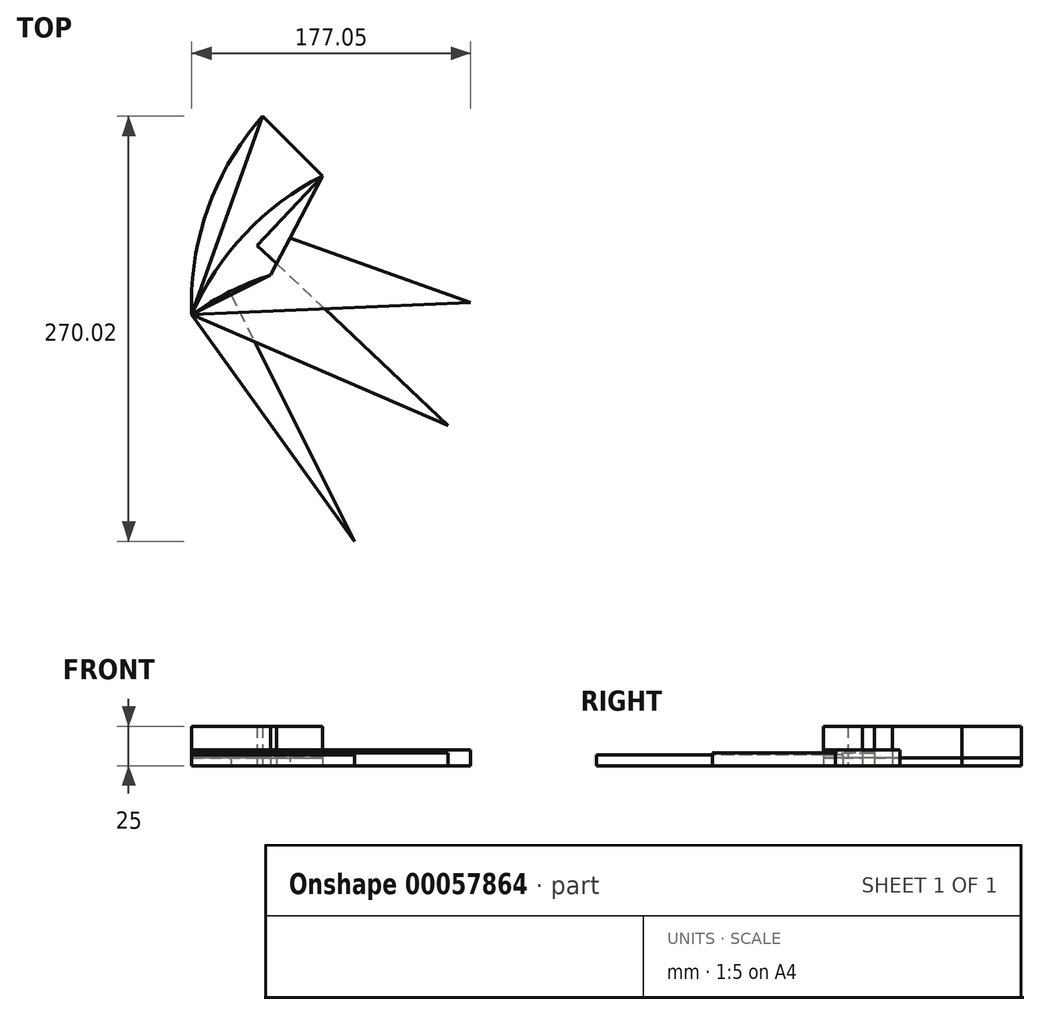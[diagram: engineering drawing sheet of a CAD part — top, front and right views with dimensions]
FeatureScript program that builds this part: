
annotation { "Feature Type Name" : "Feature", "Feature Type Description" : "" }
export const myFeature = defineFeature(function(context is Context, id is Id, definition is map)
    precondition{}
    {
        {
            var Q0;
            Q0=qCreatedBy(makeId("Top.planeOp"),FACE);
            var sketch = newSketch(context, id + "F0", { "sketchPlane" : qUnion([Q0])});
            skCircle(sketch, "E0", {"center": v(0, 0) * mm, "radius": 150 * mm});
            skLineSegment(sketch, "E1", {"start": v(0, 0) * mm, "end": v(173.9, 0) * mm});
            skLineSegment(sketch, "E2", {"start": v(0, 0) * mm, "end": v(0, 191.6) * mm});
            skPoint(sketch, "E3", {"position": v(50, 25) * mm});
            skPoint(sketch, "E4", {"position": v(83, 88) * mm});
            skLineSegment(sketch, "E5", {"start": v(0, 0) * mm, "end": v(50, 25) * mm});
            skLineSegment(sketch, "E6", {"start": v(0, 0) * mm, "end": v(83, 88) * mm});
            skPoint(sketch, "E7", {"position": v(41.5, 44) * mm});
            skPoint(sketch, "E8", {"position": v(25, 12.5) * mm});
            skLineSegment(sketch, "E9", {"start": v(25, 12.5) * mm, "end": v(103.26, -144.02) * mm});
            skLineSegment(sketch, "E10", {"start": v(41.5, 44) * mm, "end": v(162.68, -70.3) * mm});
            skLineSegment(sketch, "E11", {"start": v(0, 0) * mm, "end": v(103.26, -144.02) * mm});
            skLineSegment(sketch, "E12", {"start": v(50, 25) * mm, "end": v(103.26, -144.02) * mm, "construction": true});
            skLineSegment(sketch, "E13", {"start": v(0, 0) * mm, "end": v(162.68, -70.3) * mm});
            skLineSegment(sketch, "E14", {"start": v(83, 88) * mm, "end": v(162.68, -70.3) * mm, "construction": true});
            skArc(sketch, "E15", {"start": v(0, 0) * mm, "mid": v(24, 14.48) * mm, "end": v(50, 25) * mm});
            skArc(sketch, "E16", {"start": v(83, 88) * mm, "mid": v(33.76, 51.3) * mm, "end": v(0, 0) * mm});
            skLineSegment(sketch, "E17", {"start": v(50, 25) * mm, "end": v(83, 88) * mm});
            skLineSegment(sketch, "E18", {"start": v(50, 25) * mm, "end": v(0, 25) * mm, "construction": true});
            skLineSegment(sketch, "E19", {"start": v(83, 88) * mm, "end": v(0, 88) * mm, "construction": true});
            skLineSegment(sketch, "E20", {"start": v(50, 25) * mm, "end": v(50, 0) * mm, "construction": true});
            skLineSegment(sketch, "E21", {"start": v(83, 88) * mm, "end": v(83, 0) * mm, "construction": true});
            skPoint(sketch, "E22", {"position": v(45, 126) * mm});
            skLineSegment(sketch, "E23", {"start": v(45, 126) * mm, "end": v(0, 0) * mm});
            skPoint(sketch, "E24.positionSnap0", {"position": v(22.5, 63) * mm});
            skLineSegment(sketch, "E25", {"start": v(22.5, 63) * mm, "end": v(177.05, 7.8) * mm});
            skLineSegment(sketch, "E26", {"start": v(0, 0) * mm, "end": v(177.05, 7.8) * mm});
            skLineSegment(sketch, "E27", {"start": v(45, 126) * mm, "end": v(177.05, 7.8) * mm, "construction": true});
            skLineSegment(sketch, "E28", {"start": v(45, 126) * mm, "end": v(0, 126) * mm, "construction": true});
            skPoint(sketch, "E29.endSnap0", {"position": v(50, 12.5) * mm});
            skArc(sketch, "E30", {"start": v(0, 0) * mm, "mid": v(10.15, 67.4) * mm, "end": v(45, 126) * mm});
            skLineSegment(sketch, "E31", {"start": v(22.5, 63) * mm, "end": v(10.15, 67.4) * mm});
            skLineSegment(sketch, "E32", {"start": v(45, 126) * mm, "end": v(83, 88) * mm});
            skCircle(sketch, "E33", {"center": v(0, 0) * mm, "radius": 177.22 * mm, "construction": true});
            skPoint(sketch, "E34", {"position": v(66.5, 56.5) * mm});
            skPoint(sketch, "E35", {"position": v(64, 107) * mm});
            skLineSegment(sketch, "E36", {"start": v(66.5, 56.5) * mm, "end": v(0, 0) * mm, "construction": true});
            skLineSegment(sketch, "E37", {"start": v(64, 107) * mm, "end": v(0, 0) * mm, "construction": true});
            skPoint(sketch, "E38", {"position": v(33.25, 28.25) * mm});
            skPoint(sketch, "E39", {"position": v(32, 53.5) * mm});
            skLineSegment(sketch, "E40", {"start": v(32, 53.5) * mm, "end": v(174.37, -31.65) * mm, "construction": true});
            skLineSegment(sketch, "E41", {"start": v(33.25, 28.25) * mm, "end": v(144.46, -102.65) * mm, "construction": true});
            skLineSegment(sketch, "E42", {"start": v(0, 0) * mm, "end": v(174.37, -31.65) * mm, "construction": true});
            skLineSegment(sketch, "E43", {"start": v(0, 0) * mm, "end": v(144.46, -102.65) * mm, "construction": true});
            skSolve(sketch);
        }
        {
            var Q0;
            {var subQ3=sQuery(id+"F0.wireOp",EDGE,"E31");Q0=makeQuery(id+"F0.imprint","IMPRINT",FACE,{"disambiguationData":[TD([[makeQuery(id+"F0.imprint","IMPRINT",EDGE,{"derivedFrom":subQ3}),-1.0]])]});}
            var Q1;
            {var subQ5=sQuery(id+"F0.wireOp",EDGE,"E31");Q1=makeQuery(id+"F0.imprint","IMPRINT",FACE,{"disambiguationData":[TD([[makeQuery(id+"F0.imprint","IMPRINT",EDGE,{"derivedFrom":subQ5}),1.0]])]});}
            var Q2;
            {var subQ1=sQuery(id+"F0.wireOp",EDGE,"E6");var subQ3=makeQuery(id+"F0.imprint","INTERSECT",VERTEX,{"derivedFrom":[subQ1,sQuery(id+"F0.wireOp",EDGE,"E10")]});Q2=makeQuery(id+"F0.imprint","IMPRINT",FACE,{"disambiguationData":[TD([[makeQuery(id+"F0.imprint","IMPRINT",EDGE,{"disambiguationData":[TD([[subQ3,-1.0]])],"derivedFrom":subQ1}),1.0]])]});}
            var Q3;
            {var subQ1=sQuery(id+"F0.wireOp",EDGE,"E6");var subQ3=sQuery(id+"F0.wireOp",EDGE,"E25");var subQ4=makeQuery(id+"F0.imprint","INTERSECT",VERTEX,{"derivedFrom":[subQ1,subQ3]});Q3=makeQuery(id+"F0.imprint","IMPRINT",FACE,{"disambiguationData":[TD([[makeQuery(id+"F0.imprint","IMPRINT",EDGE,{"disambiguationData":[TD([[subQ4,1.0]])],"derivedFrom":subQ3}),1.0]])]});}
            var Q4;
            {var subQ0=sQuery(id+"F0.wireOp",EDGE,"E15");Q4=makeQuery(id+"F0.imprint","IMPRINT",FACE,{"disambiguationData":[TD([[makeQuery(id+"F0.imprint","IMPRINT",EDGE,{"derivedFrom":subQ0}),-1.0]])]});}
            extrude(context, id + "F1", {"entities" : qUnion([Q0, Q1, Q2, Q3, Q4]), "depth" : 25 * mm, "offsetDistance" : 25 * mm});
        }
        {
            var Q0;
            {var subQ0=sQuery(id+"F0.wireOp",EDGE,"E32");Q0=makeQuery(id+"F0.imprint","IMPRINT",FACE,{"disambiguationData":[TD([[makeQuery(id+"F0.imprint","IMPRINT",EDGE,{"derivedFrom":subQ0}),-1.0]])]});}
            var Q1;
            {var subQ1=sQuery(id+"F0.wireOp",EDGE,"E16");var subQ3=sQuery(id+"F0.wireOp",EDGE,"E25");var subQ4=makeQuery(id+"F0.imprint","INTERSECT",VERTEX,{"derivedFrom":[subQ1,subQ3]});Q1=makeQuery(id+"F0.imprint","IMPRINT",FACE,{"disambiguationData":[TD([[makeQuery(id+"F0.imprint","IMPRINT",EDGE,{"disambiguationData":[TD([[subQ4,1.0]])],"derivedFrom":subQ3}),-1.0]])]});}
            extrude(context, id + "F2", {"entities" : qUnion([Q0, Q1]), "depth" : 5 * mm, "offsetDistance" : 25 * mm});
        }
        {
            var Q0;
            {var subQ1=sQuery(id+"F0.wireOp",EDGE,"E6");var subQ3=sQuery(id+"F0.wireOp",EDGE,"E25");var subQ4=makeQuery(id+"F0.imprint","INTERSECT",VERTEX,{"derivedFrom":[subQ1,subQ3]});Q0=makeQuery(id+"F0.imprint","IMPRINT",FACE,{"disambiguationData":[TD([[makeQuery(id+"F0.imprint","IMPRINT",EDGE,{"disambiguationData":[TD([[subQ4,-1.0]])],"derivedFrom":subQ3}),1.0]])]});}
            var Q1;
            {var subQ0=sQuery(id+"F0.wireOp",EDGE,"E10");var subQ1=sQuery(id+"F0.wireOp",EDGE,"E6");var subQ2=makeQuery(id+"F0.imprint","INTERSECT",VERTEX,{"derivedFrom":[subQ1,subQ0]});Q1=makeQuery(id+"F0.imprint","IMPRINT",FACE,{"disambiguationData":[TD([[makeQuery(id+"F0.imprint","IMPRINT",EDGE,{"disambiguationData":[TD([[subQ2,-1.0]])],"derivedFrom":subQ1}),-1.0]])]});}
            var Q2;
            {var subQ0=sQuery(id+"F0.wireOp",EDGE,"E15");Q2=makeQuery(id+"F0.imprint","IMPRINT",FACE,{"disambiguationData":[TD([[makeQuery(id+"F0.imprint","IMPRINT",EDGE,{"derivedFrom":subQ0}),1.0]])]});}
            extrude(context, id + "F3", {"entities" : qUnion([Q0, Q1, Q2]), "depth" : 5 * mm, "offsetDistance" : 25 * mm});
        }
        {
            var Q0;
            {var subQ0=sQuery(id+"F0.wireOp",EDGE,"E11");var subQ1=sQuery(id+"F0.wireOp",EDGE,"E0");var subQ2=makeQuery(id+"F0.imprint","INTERSECT",VERTEX,{"derivedFrom":[subQ1,subQ0]});Q0=makeQuery(id+"F0.imprint","IMPRINT",FACE,{"disambiguationData":[TD([[makeQuery(id+"F0.imprint","IMPRINT",EDGE,{"disambiguationData":[TD([[subQ2,-1.0]])],"derivedFrom":subQ1}),1.0]])]});}
            var Q1;
            {var subQ1=sQuery(id+"F0.wireOp",EDGE,"E1");var subQ3=sQuery(id+"F0.wireOp",EDGE,"E9");var subQ4=makeQuery(id+"F0.imprint","INTERSECT",VERTEX,{"derivedFrom":[subQ1,subQ3]});Q1=makeQuery(id+"F0.imprint","IMPRINT",FACE,{"disambiguationData":[TD([[makeQuery(id+"F0.imprint","IMPRINT",EDGE,{"disambiguationData":[TD([[subQ4,-1.0]])],"derivedFrom":subQ3}),-1.0]])]});}
            var Q2;
            {var subQ1=sQuery(id+"F0.wireOp",EDGE,"E1");var subQ3=sQuery(id+"F0.wireOp",EDGE,"E9");var subQ4=makeQuery(id+"F0.imprint","INTERSECT",VERTEX,{"derivedFrom":[subQ1,subQ3]});Q2=makeQuery(id+"F0.imprint","IMPRINT",FACE,{"disambiguationData":[TD([[makeQuery(id+"F0.imprint","IMPRINT",EDGE,{"disambiguationData":[TD([[subQ4,1.0]])],"derivedFrom":subQ3}),-1.0]])]});}
            var Q3;
            {var subQ1=sQuery(id+"F0.wireOp",EDGE,"E5");var subQ3=sQuery(id+"F0.wireOp",EDGE,"E9");var subQ4=makeQuery(id+"F0.imprint","INTERSECT",VERTEX,{"derivedFrom":[subQ1,subQ3]});Q3=makeQuery(id+"F0.imprint","IMPRINT",FACE,{"disambiguationData":[TD([[makeQuery(id+"F0.imprint","IMPRINT",EDGE,{"disambiguationData":[TD([[subQ4,-1.0]])],"derivedFrom":subQ3}),-1.0]])]});}
            var Q4;
            {var subQ0=sQuery(id+"F0.wireOp",EDGE,"E11");var subQ1=sQuery(id+"F0.wireOp",EDGE,"E0");var subQ2=makeQuery(id+"F0.imprint","INTERSECT",VERTEX,{"derivedFrom":[subQ1,subQ0]});Q4=makeQuery(id+"F0.imprint","IMPRINT",FACE,{"disambiguationData":[TD([[makeQuery(id+"F0.imprint","IMPRINT",EDGE,{"disambiguationData":[TD([[subQ2,-1.0]])],"derivedFrom":subQ1}),-1.0]])]});}
            extrude(context, id + "F4", {"entities" : qUnion([Q0, Q1, Q2, Q3, Q4]), "depth" : 7 * mm, "offsetDistance" : 25 * mm});
        }
        {
            var Q0;
            {var subQ3=sQuery(id+"F0.wireOp",EDGE,"E13");var subQ7=sQuery(id+"F0.wireOp",EDGE,"E0");var subQ8=makeQuery(id+"F0.imprint","INTERSECT",VERTEX,{"derivedFrom":[subQ7,subQ3]});Q0=makeQuery(id+"F0.imprint","IMPRINT",FACE,{"disambiguationData":[TD([[makeQuery(id+"F0.imprint","IMPRINT",EDGE,{"disambiguationData":[TD([[subQ8,-1.0]])],"derivedFrom":subQ7}),1.0]])]});}
            var Q1;
            {var subQ0=sQuery(id+"F0.wireOp",EDGE,"E13");var subQ1=sQuery(id+"F0.wireOp",EDGE,"E0");var subQ2=makeQuery(id+"F0.imprint","INTERSECT",VERTEX,{"derivedFrom":[subQ1,subQ0]});Q1=makeQuery(id+"F0.imprint","IMPRINT",FACE,{"disambiguationData":[TD([[makeQuery(id+"F0.imprint","IMPRINT",EDGE,{"disambiguationData":[TD([[subQ2,-1.0]])],"derivedFrom":subQ1}),-1.0]])]});}
            var Q2;
            {var subQ1=sQuery(id+"F0.wireOp",EDGE,"E1");var subQ3=sQuery(id+"F0.wireOp",EDGE,"E9");var subQ4=makeQuery(id+"F0.imprint","INTERSECT",VERTEX,{"derivedFrom":[subQ1,subQ3]});Q2=makeQuery(id+"F0.imprint","IMPRINT",FACE,{"disambiguationData":[TD([[makeQuery(id+"F0.imprint","IMPRINT",EDGE,{"disambiguationData":[TD([[subQ4,-1.0]])],"derivedFrom":subQ3}),-1.0]])]});}
            var Q3;
            {var subQ1=sQuery(id+"F0.wireOp",EDGE,"E5");var subQ3=sQuery(id+"F0.wireOp",EDGE,"E9");var subQ4=makeQuery(id+"F0.imprint","INTERSECT",VERTEX,{"derivedFrom":[subQ1,subQ3]});Q3=makeQuery(id+"F0.imprint","IMPRINT",FACE,{"disambiguationData":[TD([[makeQuery(id+"F0.imprint","IMPRINT",EDGE,{"disambiguationData":[TD([[subQ4,-1.0]])],"derivedFrom":subQ3}),-1.0]])]});}
            var Q4;
            {var subQ1=sQuery(id+"F0.wireOp",EDGE,"E5");var subQ5=sQuery(id+"F0.wireOp",EDGE,"E9");var subQ6=makeQuery(id+"F0.imprint","INTERSECT",VERTEX,{"derivedFrom":[subQ1,subQ5]});Q4=makeQuery(id+"F0.imprint","IMPRINT",FACE,{"disambiguationData":[TD([[makeQuery(id+"F0.imprint","IMPRINT",EDGE,{"disambiguationData":[TD([[subQ6,-1.0]])],"derivedFrom":subQ5}),1.0]])]});}
            var Q5;
            {var subQ0=sQuery(id+"F0.wireOp",EDGE,"E9");var subQ1=sQuery(id+"F0.wireOp",EDGE,"E1");var subQ2=makeQuery(id+"F0.imprint","INTERSECT",VERTEX,{"derivedFrom":[subQ1,subQ0]});Q5=makeQuery(id+"F0.imprint","IMPRINT",FACE,{"disambiguationData":[TD([[makeQuery(id+"F0.imprint","IMPRINT",EDGE,{"disambiguationData":[TD([[subQ2,-1.0]])],"derivedFrom":subQ1}),1.0]])]});}
            var Q6;
            {var subQ1=sQuery(id+"F0.wireOp",EDGE,"E1");var subQ3=sQuery(id+"F0.wireOp",EDGE,"E9");var subQ4=makeQuery(id+"F0.imprint","INTERSECT",VERTEX,{"derivedFrom":[subQ1,subQ3]});Q6=makeQuery(id+"F0.imprint","IMPRINT",FACE,{"disambiguationData":[TD([[makeQuery(id+"F0.imprint","IMPRINT",EDGE,{"disambiguationData":[TD([[subQ4,1.0]])],"derivedFrom":subQ3}),-1.0]])]});}
            extrude(context, id + "F5", {"entities" : qUnion([Q0, Q1, Q2, Q3, Q4, Q5, Q6]), "depth" : 8 * mm, "offsetDistance" : 25 * mm});
        }
        {
            var Q0;
            {var subQ1=sQuery(id+"F0.wireOp",EDGE,"E5");var subQ3=sQuery(id+"F0.wireOp",EDGE,"E9");var subQ4=makeQuery(id+"F0.imprint","INTERSECT",VERTEX,{"derivedFrom":[subQ1,subQ3]});Q0=makeQuery(id+"F0.imprint","IMPRINT",FACE,{"disambiguationData":[TD([[makeQuery(id+"F0.imprint","IMPRINT",EDGE,{"disambiguationData":[TD([[subQ4,-1.0]])],"derivedFrom":subQ3}),-1.0]])]});}
            var Q1;
            {var subQ1=sQuery(id+"F0.wireOp",EDGE,"E5");var subQ5=sQuery(id+"F0.wireOp",EDGE,"E9");var subQ6=makeQuery(id+"F0.imprint","INTERSECT",VERTEX,{"derivedFrom":[subQ1,subQ5]});Q1=makeQuery(id+"F0.imprint","IMPRINT",FACE,{"disambiguationData":[TD([[makeQuery(id+"F0.imprint","IMPRINT",EDGE,{"disambiguationData":[TD([[subQ6,-1.0]])],"derivedFrom":subQ5}),1.0]])]});}
            var Q2;
            {var subQ5=sQuery(id+"F0.wireOp",EDGE,"E26");var subQ6=sQuery(id+"F0.wireOp",EDGE,"E0");var subQ7=makeQuery(id+"F0.imprint","INTERSECT",VERTEX,{"derivedFrom":[subQ6,subQ5]});Q2=makeQuery(id+"F0.imprint","IMPRINT",FACE,{"disambiguationData":[TD([[makeQuery(id+"F0.imprint","IMPRINT",EDGE,{"disambiguationData":[TD([[subQ7,-1.0]])],"derivedFrom":subQ6}),1.0]])]});}
            var Q3;
            {var subQ0=sQuery(id+"F0.wireOp",EDGE,"E26");var subQ1=sQuery(id+"F0.wireOp",EDGE,"E0");var subQ2=makeQuery(id+"F0.imprint","INTERSECT",VERTEX,{"derivedFrom":[subQ1,subQ0]});Q3=makeQuery(id+"F0.imprint","IMPRINT",FACE,{"disambiguationData":[TD([[makeQuery(id+"F0.imprint","IMPRINT",EDGE,{"disambiguationData":[TD([[subQ2,-1.0]])],"derivedFrom":subQ1}),-1.0]])]});}
            extrude(context, id + "F6", {"entities" : qUnion([Q0, Q1, Q2, Q3]), "depth" : 10 * mm, "offsetDistance" : 25 * mm});
        }
    });
